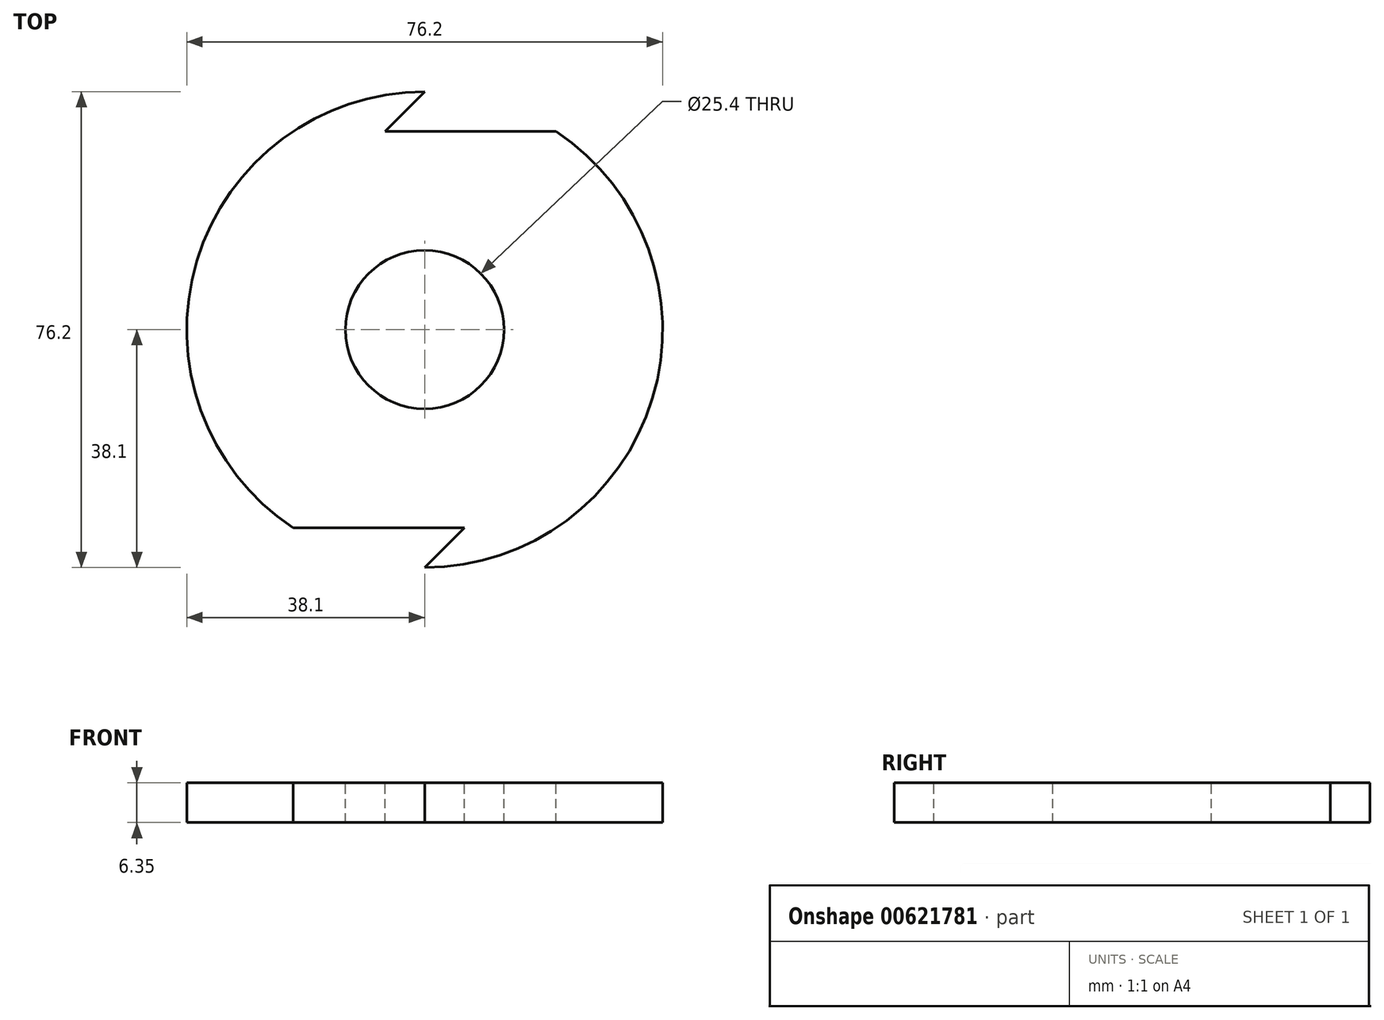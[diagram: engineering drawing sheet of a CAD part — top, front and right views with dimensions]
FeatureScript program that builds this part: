
annotation { "Feature Type Name" : "Feature", "Feature Type Description" : "" }
export const myFeature = defineFeature(function(context is Context, id is Id, definition is map)
    precondition{}
    {
        {
            var Q0;
            Q0=qCreatedBy(makeId("Top.planeOp"),FACE);
            var sketch = newSketch(context, id + "F0", { "sketchPlane" : qUnion([Q0])});
            skCircle(sketch, "E0", {"center": v(0, 0) * mm, "radius": 38.1 * mm});
            skLineSegment(sketch, "E1", {"start": v(0, 0) * mm, "end": v(0, 0) * mm});
            skLineSegment(sketch, "E2", {"start": v(0, -38.1) * mm, "end": v(0, 38.1) * mm, "construction": true});
            skLineSegment(sketch, "E3", {"start": v(0, 38.1) * mm, "end": v(0, 38.1) * mm});
            skLineSegment(sketch, "E4", {"start": v(38.1, 0) * mm, "end": v(-38.1, 0) * mm, "construction": true});
            skLineSegment(sketch, "E5", {"start": v(0, 31.75) * mm, "end": v(0, 31.75) * mm});
            skLineSegment(sketch, "E6", {"start": v(0, 31.75) * mm, "end": v(0, 38.1) * mm});
            skLineSegment(sketch, "E7", {"start": v(0, 31.75) * mm, "end": v(21.06, 31.75) * mm});
            skLineSegment(sketch, "E8", {"start": v(31.75, 0) * mm, "end": v(31.75, 6.35) * mm});
            skLineSegment(sketch, "E9", {"start": v(31.75, 6.35) * mm, "end": v(38.1, 0) * mm});
            skLineSegment(sketch, "E10", {"start": v(31.75, 6.35) * mm, "end": v(31.75, -21.06) * mm});
            skLineSegment(sketch, "E11", {"start": v(31.75, -21.06) * mm, "end": v(31.75, -21.06) * mm});
            skLineSegment(sketch, "E12", {"start": v(0, -31.75) * mm, "end": v(6.35, -31.75) * mm});
            skLineSegment(sketch, "E13", {"start": v(6.35, -31.75) * mm, "end": v(0, -38.1) * mm});
            skLineSegment(sketch, "E14", {"start": v(0, -31.75) * mm, "end": v(-21.06, -31.75) * mm});
            skCircle(sketch, "E15", {"center": v(0, 0) * mm, "radius": 12.7 * mm});
            skLineSegment(sketch, "E16", {"start": v(-38.1, 0) * mm, "end": v(-31.75, -6.35) * mm});
            skLineSegment(sketch, "E17", {"start": v(-31.75, -6.35) * mm, "end": v(-31.75, 0) * mm});
            skLineSegment(sketch, "E18", {"start": v(-31.75, 0) * mm, "end": v(-31.75, 21.06) * mm});
            skLineSegment(sketch, "E19", {"start": v(0, 31.75) * mm, "end": v(-6.35, 31.75) * mm});
            skLineSegment(sketch, "E20", {"start": v(-6.35, 31.75) * mm, "end": v(0, 38.1) * mm});
            skLineSegment(sketch, "E21", {"start": v(0, -38.1) * mm, "end": v(-38.1, 0) * mm, "construction": true});
            skLineSegment(sketch, "E22", {"start": v(-41.8, -3.7) * mm, "end": v(0, 38.1) * mm, "construction": true});
            skLineSegment(sketch, "E23", {"start": v(0, 38.1) * mm, "end": v(38.1, 0) * mm, "construction": true});
            skLineSegment(sketch, "E24", {"start": v(38.1, 0) * mm, "end": v(0, -38.1) * mm, "construction": true});
            skLineSegment(sketch, "E25", {"start": v(-20.9, 17.2) * mm, "end": v(-20.9, 17.2) * mm});
            skLineSegment(sketch, "E26", {"start": v(0, 0) * mm, "end": v(26.94, 26.94) * mm, "construction": true});
            skLineSegment(sketch, "E27", {"start": v(0, 0) * mm, "end": v(26.65, -27.23) * mm, "construction": true});
            skLineSegment(sketch, "E28", {"start": v(0, 0) * mm, "end": v(-26.94, -26.94) * mm, "construction": true});
            skLineSegment(sketch, "E29", {"start": v(0, 0) * mm, "end": v(-26.94, 26.94) * mm, "construction": true});
            skLineSegment(sketch, "E30", {"start": v(-26.94, 26.94) * mm, "end": v(-26.94, 26.94) * mm});
            skLineSegment(sketch, "E31", {"start": v(-26.94, -26.94) * mm, "end": v(-22.45, -22.45) * mm, "construction": true});
            skLineSegment(sketch, "E32", {"start": v(-22.45, -22.45) * mm, "end": v(-37.34, -7.56) * mm});
            skLineSegment(sketch, "E33", {"start": v(-22.45, -22.45) * mm, "end": v(-17.96, -26.94) * mm});
            skLineSegment(sketch, "E34", {"start": v(-17.96, -26.94) * mm, "end": v(-26.94, -26.94) * mm});
            skLineSegment(sketch, "E35", {"start": v(-26.94, 26.94) * mm, "end": v(-22.45, 22.45) * mm, "construction": true});
            skLineSegment(sketch, "E36", {"start": v(-22.45, 22.45) * mm, "end": v(-26.94, 17.96) * mm});
            skLineSegment(sketch, "E37", {"start": v(-26.94, 17.96) * mm, "end": v(-26.94, 26.94) * mm});
            skLineSegment(sketch, "E38", {"start": v(-22.45, 22.45) * mm, "end": v(-7.56, 37.34) * mm});
            skLineSegment(sketch, "E39", {"start": v(22.45, 22.45) * mm, "end": v(17.96, 26.94) * mm});
            skLineSegment(sketch, "E40", {"start": v(17.96, 26.94) * mm, "end": v(26.94, 26.94) * mm});
            skLineSegment(sketch, "E41", {"start": v(22.45, 22.45) * mm, "end": v(37.34, 7.56) * mm});
            skLineSegment(sketch, "E42", {"start": v(26.65, -27.23) * mm, "end": v(22.2, -22.69) * mm, "construction": true});
            skLineSegment(sketch, "E43", {"start": v(22.2, -22.69) * mm, "end": v(26.75, -18.25) * mm});
            skLineSegment(sketch, "E44", {"start": v(26.75, -18.25) * mm, "end": v(26.65, -27.23) * mm});
            skLineSegment(sketch, "E45", {"start": v(22.2, -22.69) * mm, "end": v(7.16, -37.42) * mm});
            skSolve(sketch);
        }
        {
            var Q0;
            Q0=makeQuery(id+"F0.imprint","IMPRINT",FACE,{"disambiguationData":[TD([[makeQuery(id+"F0.imprint","IMPRINT",EDGE,{"derivedFrom":sQuery(id+"F0.wireOp",EDGE,"E39")}),-1.0]])]});
            var Q1;
            {var subQ0=sQuery(id+"F0.wireOp",EDGE,"E32");Q1=makeQuery(id+"F0.imprint","IMPRINT",FACE,{"disambiguationData":[TD([[makeQuery(id+"F0.imprint","IMPRINT",EDGE,{"derivedFrom":subQ0}),1.0]])]});}
            var Q2;
            Q2=makeQuery(id+"F0.imprint","IMPRINT",FACE,{"disambiguationData":[TD([[makeQuery(id+"F0.imprint","IMPRINT",EDGE,{"derivedFrom":sQuery(id+"F0.wireOp",EDGE,"E43")}),-1.0]])]});
            var Q3;
            Q3=makeQuery(id+"F0.imprint","IMPRINT",FACE,{"disambiguationData":[TD([[makeQuery(id+"F0.imprint","IMPRINT",EDGE,{"derivedFrom":sQuery(id+"F0.wireOp",EDGE,"E36")}),-1.0]])]});
            var Q4;
            {var subQ10=sQuery(id+"F0.wireOp",EDGE,"E7");Q4=makeQuery(id+"F0.imprint","IMPRINT",FACE,{"disambiguationData":[TD([[makeQuery(id+"F0.imprint","IMPRINT",EDGE,{"derivedFrom":subQ10}),-1.0]])]});}
            var Q5;
            {var subQ0=sQuery(id+"F0.wireOp",EDGE,"E9");Q5=makeQuery(id+"F0.imprint","IMPRINT",FACE,{"disambiguationData":[TD([[makeQuery(id+"F0.imprint","IMPRINT",EDGE,{"derivedFrom":subQ0}),-1.0]])]});}
            var Q6;
            {var subQ0=sQuery(id+"F0.wireOp",EDGE,"E16");Q6=makeQuery(id+"F0.imprint","IMPRINT",FACE,{"disambiguationData":[TD([[makeQuery(id+"F0.imprint","IMPRINT",EDGE,{"derivedFrom":subQ0}),1.0]])]});}
            extrude(context, id + "F1", {"entities" : qUnion([Q0, Q1, Q2, Q3, Q4, Q5, Q6]), "oppositeDirection" : true, "depth" : 6.35 * mm, "offsetDistance" : 25.4 * mm});
        }
    });
